# Revit family: kaffeemaschine_mit_kanne_angepasst
name_source: partatom
category: Möbel
units: mm (PartAtom-declared; Revit-internal decimal feet)

## family parameters
Arbeitsebenenbasiert = Nein
Beim Laden mit Abzugskörper schneiden = Nein
Gemeinsam genutzt = Nein
Immer vertikal = Ja
Raumberechnungspunkt = Nein

## types (4) — shared parameters
B2_hinten = 140 mm
zero-valued in all types: Vorgabe-Ansicht

## per-type parameters (varying)
| type | Breite | Höhe | Höhe2_unten | Höhe_Zwischenraum | Kanne sichtbar | Tiefe |
| Kaffeemaschine klein | 200 mm  [stored 0.656168 ft] | 400 mm  [stored 1.31234 ft] | 40 mm  [stored 0.131234 ft] | 330 mm | Ja | 400 mm  [stored 1.31234 ft] |
| Kaffeemaschine gross | 250 mm  [stored 0.82021 ft] | 500 mm  [stored 1.64042 ft] | 50 mm  [stored 0.164042 ft] | 410 mm | Ja | 450 mm  [stored 1.47638 ft] |
| Kaffeemaschine mini | 200 mm  [stored 0.656168 ft] | 400 mm  [stored 1.31234 ft] | 40 mm  [stored 0.131234 ft] | 300 mm | Ja | 400 mm  [stored 1.31234 ft] |
| Kaffeemaschine gross ohne Kanne | 250 mm  [stored 0.82021 ft] | 500 mm  [stored 1.64042 ft] | 50 mm  [stored 0.164042 ft] | 410 mm | Nein | 450 mm  [stored 1.47638 ft] |

note: [stored X ft] marks values corroborated as IEEE doubles in the binary element streams (Revit-internal decimal feet)
